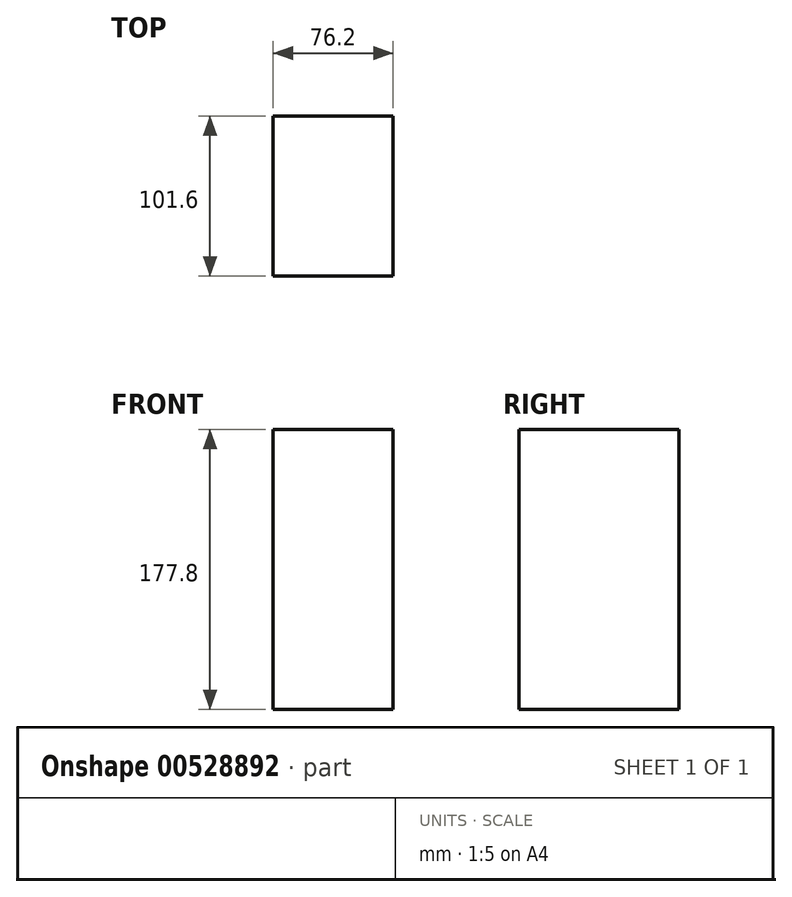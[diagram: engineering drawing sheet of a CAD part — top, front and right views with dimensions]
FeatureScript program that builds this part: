
annotation { "Feature Type Name" : "Feature", "Feature Type Description" : "" }
export const myFeature = defineFeature(function(context is Context, id is Id, definition is map)
    precondition{}
    {
        {
            var Q0;
            Q0=qCreatedBy(makeId("Top.planeOp"),FACE);
            var sketch = newSketch(context, id + "F0", { "sketchPlane" : qUnion([Q0])});
            skLineSegment(sketch, "E0.bottom", {"start": v(-38.1, 50.8) * mm, "end": v(38.1, 50.8) * mm});
            skLineSegment(sketch, "E0.top", {"start": v(-38.1, -50.8) * mm, "end": v(38.1, -50.8) * mm});
            skLineSegment(sketch, "E0.left", {"start": v(-38.1, 50.8) * mm, "end": v(-38.1, -50.8) * mm});
            skLineSegment(sketch, "E0.right", {"start": v(38.1, 50.8) * mm, "end": v(38.1, -50.8) * mm});
            skLineSegment(sketch, "E1", {"start": v(38.1, 50.8) * mm, "end": v(-38.1, -50.8) * mm});
            skSolve(sketch);
        }
        {
            var Q0;
            Q0 = qSketchRegion(id + "F0", true);
            extrude(context, id + "F1", {"entities" : qUnion([Q0]), "endBound" : BoundingType.SYMMETRIC, "depth" : 177.8 * mm, "offsetDistance" : 25.4 * mm});
        }
    });
